FCSTD DOCUMENT  (FreeCAD 0.16R6710 (Git))
Label: holes_test
License: All rights reserved
LicenseURL: http://en.wikipedia.org/wiki/All_rights_reserved
objects: Sketcher::SketchObject×1
note: 1 computed .brp shape members not serialized (recipe doc carries the construction recipe); baked Part::Feature solids carry a one-line shape summary decoded from their .brp

FEATURE [Sketcher::SketchObject] Sketch
  sketch-geometry (13):
    g0: Circle CenterX=-15.5475 CenterY=0 CenterZ=0 NormalX=0 NormalY=0 NormalZ=1 Radius=1.2
    g1: Circle CenterX=-11.3932 CenterY=0 CenterZ=0 NormalX=0 NormalY=0 NormalZ=1 Radius=1.25
    g2: Circle CenterX=-7.23204 CenterY=0 CenterZ=0 NormalX=0 NormalY=0 NormalZ=1 Radius=1.3
    g3: Circle CenterX=-2.61156 CenterY=0 CenterZ=0 NormalX=0 NormalY=0 NormalZ=1 Radius=1.35
    g4: Circle CenterX=1.72009 CenterY=0 CenterZ=0 NormalX=0 NormalY=0 NormalZ=1 Radius=1.4
    g5: Circle CenterX=6.45241 CenterY=0 CenterZ=0 NormalX=0 NormalY=0 NormalZ=1 Radius=1.45
    g6: LineSegment [constr] StartX=-27.4769 StartY=-6.1615 StartZ=0 EndX=22.737 EndY=-6.1615 EndZ=0
    g7: Circle CenterX=-4.47182 CenterY=-6.1615 CenterZ=0 NormalX=0 NormalY=0 NormalZ=1 Radius=3.5
    g8: Circle CenterX=-12.7359 CenterY=-6.1615 CenterZ=0 NormalX=0 NormalY=0 NormalZ=1 Radius=3.45
    g9: Circle CenterX=-20.764 CenterY=-6.1615 CenterZ=0 NormalX=0 NormalY=0 NormalZ=1 Radius=3.4
    g10: Circle CenterX=3.06058 CenterY=-6.1615 CenterZ=0 NormalX=0 NormalY=0 NormalZ=1 Radius=3.55
    g11: Circle CenterX=10.6999 CenterY=-6.1615 CenterZ=0 NormalX=0 NormalY=0 NormalZ=1 Radius=3.6
    g12: Circle CenterX=19.0435 CenterY=-6.1615 CenterZ=0 NormalX=0 NormalY=0 NormalZ=1 Radius=3.65
  constraints (25):
    c: PointOnObject(g0,g-1)
    c: PointOnObject(g1,g-1)
    c: PointOnObject(g2,g-1)
    c: Radius(g0) = 1.2
    c: Radius(g1) = 1.25
    c: Radius(g2) = 1.3
    c: PointOnObject(g3,g-1)
    c: Radius(g3) = 1.35
    c: PointOnObject(g4,g-1)
    c: Radius(g4) = 1.4
    c: PointOnObject(g5,g-1)
    c: Radius(g5) = 1.45
    c: Horizontal(g6)
    c: PointOnObject(g7,g6)
    c: Radius(g7) = 3.5
    c: PointOnObject(g8,g6)
    c: Radius(g8) = 3.45
    c: PointOnObject(g9,g6)
    c: Radius(g9) = 3.4
    c: PointOnObject(g10,g6)
    c: Radius(g10) = 3.55
    c: PointOnObject(g11,g6)
    c: Radius(g11) = 3.6
    c: PointOnObject(g12,g6)
    c: Radius(g12) = 3.65
